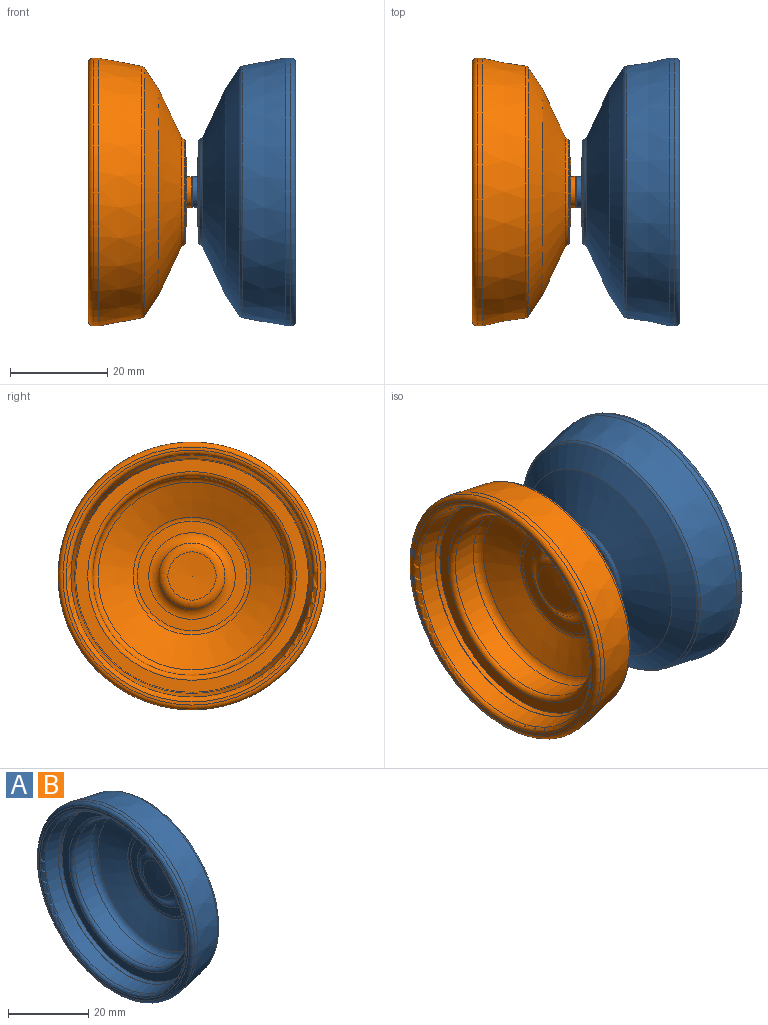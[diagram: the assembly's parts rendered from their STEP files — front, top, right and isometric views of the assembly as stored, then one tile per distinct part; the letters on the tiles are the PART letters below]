
ASSEMBLY  parts=2 mates=1
PART A: 42 faces, bbox 21.5x59.5x59.5 mm
  f0: cone r=9.65mm half-angle=0.1deg, axis (1,0,0), area 45.5mm2, adj f1,f32
  f1: torus R=9.91mm, axis (1,0,0), area 24.4mm2, adj f0,f2
  f2: plane 20.66x20.66mm, normal (1,0,0), area 26.8mm2, adj f1,f35
  f3: cone r=10.56mm half-angle=39.2deg, axis (-1,0,0), area 55.2mm2, adj f4,f35
  f4: cone r=11.22mm half-angle=64.9deg, axis (-1,0,0), area 1099.8mm2, adj f3,f5
  f5: cone r=21.05mm half-angle=56.2deg, axis (-1,0,0), area 771.2mm2, adj f4,f36
  f6: cone r=25.79mm half-angle=10.5deg, axis (-1,0,0), area 1506.5mm2, adj f7,f36
  f7: cylinder r=27.5mm len=55mm, axis (1,0,0), area 189.2mm2, adj f6,f33
  f8: plane 53x53mm, normal (-1,0,0), area 107mm2, adj f33,f34
  f9: cone r=25.02mm half-angle=10.5deg, axis (-1,0,0), area 594.5mm2, adj f34,f37
  f10: cone r=23.9mm half-angle=13.9deg, axis (-1,0,0), area 157.1mm2, adj f11,f37
  f11: plane 47.8x47.8mm, normal (-1,0,0), area 354.5mm2, adj f10,f38
  f12: cylinder r=20.41mm len=40.82mm, axis (1,0,0), area 667.7mm2, adj f38,f39
  f13: cone r=11.68mm half-angle=64.9deg, axis (-1,0,0), area 780.6mm2, adj f39,f40
  f14: plane 22.46x22.46mm, normal (-1,0,0), area 147.9mm2, adj f15,f40
  f15: torus R=8.89mm, axis (1,0,0), area 119.7mm2, adj f14,f41
  f16: torus R=0.63mm, axis (1,0,0), area 77.1mm2, adj f41
  f17: cone r=1.75mm half-angle=59deg, axis (1,0,0), area 11.3mm2, adj f18
  f18: cylinder r=1.75mm len=3.51mm, axis (1,0,0), area 35.2mm2, adj f17,f19
  f19: plane 5.93x5.93mm, normal (1,0,0), area 17.9mm2, adj f18,f20
  f20: torus R=2.97mm, axis (1,0,0), area 3mm2, adj f19,f21
  f21: cone r=3.09mm half-angle=18.4deg, axis (-1,0,0), area 5.9mm2, adj f20,f22
  f22: torus R=3.06mm, axis (1,0,0), area 0.8mm2, adj f21,f23
  f23: cylinder r=3.19mm len=6.37mm, axis (1,0,0), area 29.5mm2, adj f22,f24
  f24: plane 8x8mm, normal (1,0,0), area 18.3mm2, adj f23,f25
  f25: cylinder r=4mm len=8mm, axis (1,0,0), area 17.4mm2, adj f24,f26
  f26: plane 12.98x12.98mm, normal (1,0,0), area 82.2mm2, adj f25,f27
  f27: cylinder r=6.49mm len=12.98mm, axis (1,0,0), area 46.1mm2, adj f26,f28
  f28: torus R=6.62mm, axis (1,0,0), area 8.2mm2, adj f27,f29
  f29: plane 13.79x13.79mm, normal (1,0,0), area 11.8mm2, adj f28,f30
  f30: torus R=6.9mm, axis (1,0,0), area 17.7mm2, adj f29,f31
  f31: cylinder r=7.15mm len=14.3mm, axis (1,0,0), area 45.2mm2, adj f30,f32
  f32: plane 19.3x19.3mm, normal (1,0,0), area 132mm2, adj f0,f31
  f33: torus R=26.5mm, axis (1,0,0), area 267.8mm2, adj f7,f8
  f34: torus R=25.85mm, axis (1,0,0), area 220.2mm2, adj f8,f9
  f35: torus R=10.33mm, axis (1,0,0), area 29.3mm2, adj f2,f3
  f36: torus R=24.88mm, axis (-1,0,0), area 128.8mm2, adj f5,f6
  f37: torus R=23.18mm, axis (1,0,0), area 9mm2, adj f9,f10
  f38: torus R=21.41mm, axis (1,0,0), area 205mm2, adj f11,f12
  f39: torus R=18.41mm, axis (1,0,0), area 284.8mm2, adj f12,f13
  f40: torus R=11.23mm, axis (-1,0,0), area 64.2mm2, adj f13,f14
  f41: torus R=5.16mm, axis (-1,0,0), area 77.8mm2, adj f15,f16
PART B: same geometry as A
PLACE A rot(axis=(0,1,0),180deg) t=(49.43,9.75,-5.56)mm
PLACE B t=(41.34,9.75,-5.56)mm
MATE cylindrical A.f0 <-> B.f0  axis (-1,0,0) through (45.18,9.75,-5.56)mm
